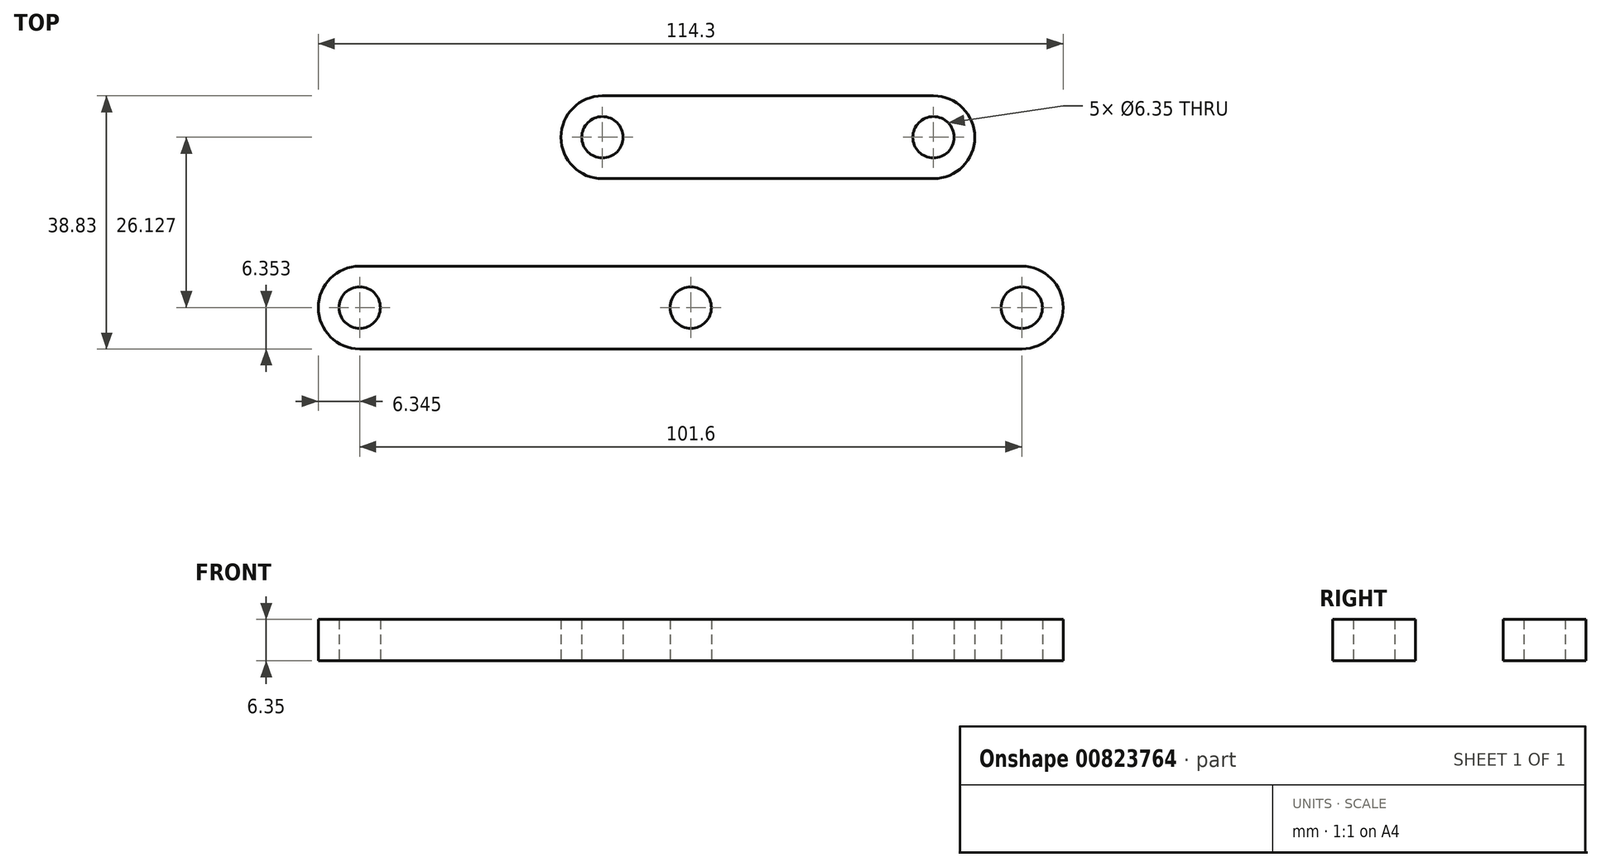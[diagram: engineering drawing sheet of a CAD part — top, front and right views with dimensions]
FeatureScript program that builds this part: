
annotation { "Feature Type Name" : "Feature", "Feature Type Description" : "" }
export const myFeature = defineFeature(function(context is Context, id is Id, definition is map)
    precondition{}
    {
        {
            var Q0;
            Q0=qCreatedBy(makeId("Top.planeOp"),FACE);
            var sketch = newSketch(context, id + "F0", { "sketchPlane" : qUnion([Q0])});
            skCircle(sketch, "E0", {"center": v(-12.33, 6.35) * mm, "radius": 6.35 * mm});
            skCircle(sketch, "E1", {"center": v(38.47, 6.35) * mm, "radius": 6.35 * mm});
            skLineSegment(sketch, "E2", {"start": v(-12.33, 12.7) * mm, "end": v(38.47, 12.7) * mm});
            skLineSegment(sketch, "E3", {"start": v(38.47, 0) * mm, "end": v(-12.33, 0) * mm});
            skCircle(sketch, "E4", {"center": v(-12.33, 6.35) * mm, "radius": 3.18 * mm});
            skCircle(sketch, "E5", {"center": v(38.47, 6.35) * mm, "radius": 3.18 * mm});
            skCircle(sketch, "E6", {"center": v(-49.58, -19.78) * mm, "radius": 6.35 * mm});
            skCircle(sketch, "E7", {"center": v(-49.58, -19.78) * mm, "radius": 3.18 * mm});
            skCircle(sketch, "E8", {"center": v(1.22, -19.78) * mm, "radius": 6.35 * mm});
            skCircle(sketch, "E9", {"center": v(1.22, -19.78) * mm, "radius": 3.18 * mm});
            skCircle(sketch, "E10", {"center": v(52.02, -19.78) * mm, "radius": 6.35 * mm});
            skCircle(sketch, "E11", {"center": v(52.02, -19.78) * mm, "radius": 3.18 * mm});
            skLineSegment(sketch, "E12", {"start": v(-49.58, -13.43) * mm, "end": v(1.22, -13.43) * mm});
            skLineSegment(sketch, "E13", {"start": v(1.22, -13.43) * mm, "end": v(52.02, -13.43) * mm});
            skLineSegment(sketch, "E14", {"start": v(52.02, -26.13) * mm, "end": v(1.22, -26.13) * mm});
            skLineSegment(sketch, "E15", {"start": v(1.22, -26.13) * mm, "end": v(-49.58, -26.13) * mm});
            skSolve(sketch);
        }
        {
            var Q0;
            Q0=makeQuery(id+"F0.imprint","IMPRINT",FACE,{"disambiguationData":[TD([[makeQuery(id+"F0.imprint","IMPRINT",EDGE,{"derivedFrom":sQuery(id+"F0.wireOp",EDGE,"E4")}),-1.0]])]});
            var Q1;
            {var subQ0=sQuery(id+"F0.wireOp",EDGE,"E2");Q1=makeQuery(id+"F0.imprint","IMPRINT",FACE,{"disambiguationData":[TD([[makeQuery(id+"F0.imprint","IMPRINT",EDGE,{"derivedFrom":subQ0}),-1.0]])]});}
            var Q2;
            Q2=makeQuery(id+"F0.imprint","IMPRINT",FACE,{"disambiguationData":[TD([[makeQuery(id+"F0.imprint","IMPRINT",EDGE,{"derivedFrom":sQuery(id+"F0.wireOp",EDGE,"E5")}),-1.0]])]});
            var Q3;
            {var subQ0=sQuery(id+"F0.wireOp",EDGE,"E12");Q3=makeQuery(id+"F0.imprint","IMPRINT",FACE,{"disambiguationData":[TD([[makeQuery(id+"F0.imprint","IMPRINT",EDGE,{"derivedFrom":subQ0}),-1.0]])]});}
            var Q4;
            {var subQ0=sQuery(id+"F0.wireOp",EDGE,"E13");Q4=makeQuery(id+"F0.imprint","IMPRINT",FACE,{"disambiguationData":[TD([[makeQuery(id+"F0.imprint","IMPRINT",EDGE,{"derivedFrom":subQ0}),-1.0]])]});}
            var Q5;
            Q5=makeQuery(id+"F0.imprint","IMPRINT",FACE,{"disambiguationData":[TD([[makeQuery(id+"F0.imprint","IMPRINT",EDGE,{"derivedFrom":sQuery(id+"F0.wireOp",EDGE,"E11")}),-1.0]])]});
            var Q6;
            Q6=makeQuery(id+"F0.imprint","IMPRINT",FACE,{"disambiguationData":[TD([[makeQuery(id+"F0.imprint","IMPRINT",EDGE,{"derivedFrom":sQuery(id+"F0.wireOp",EDGE,"E9")}),-1.0]])]});
            var Q7;
            Q7=makeQuery(id+"F0.imprint","IMPRINT",FACE,{"disambiguationData":[TD([[makeQuery(id+"F0.imprint","IMPRINT",EDGE,{"derivedFrom":sQuery(id+"F0.wireOp",EDGE,"E7")}),-1.0]])]});
            extrude(context, id + "F1", {"entities" : qUnion([Q0, Q1, Q2, Q3, Q4, Q5, Q6, Q7]), "depth" : 6.35 * mm, "offsetDistance" : 25.4 * mm});
        }
    });
